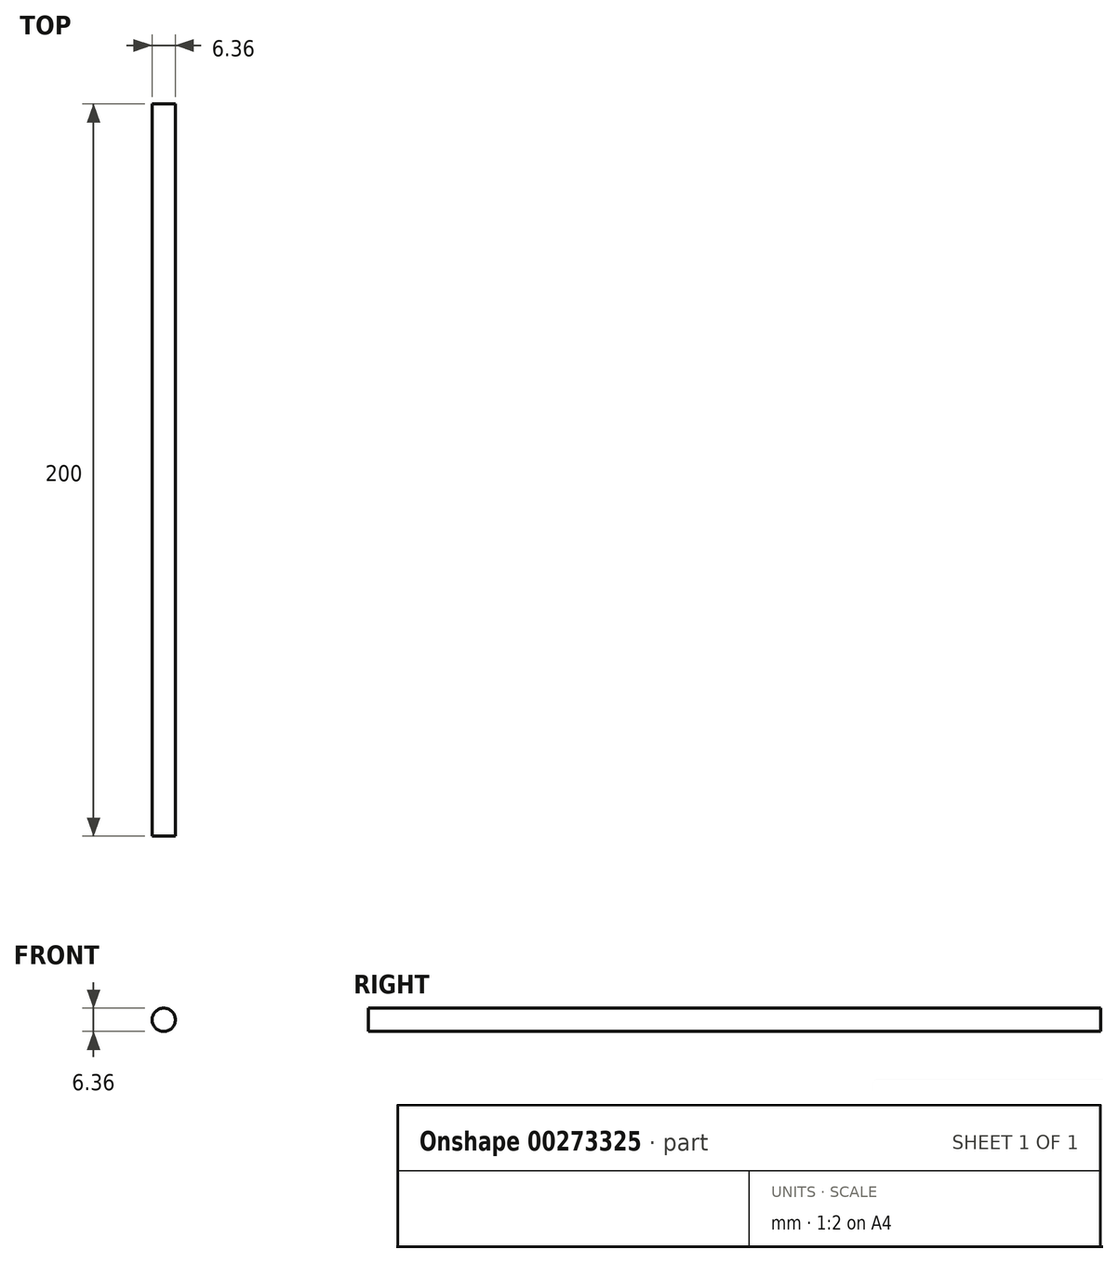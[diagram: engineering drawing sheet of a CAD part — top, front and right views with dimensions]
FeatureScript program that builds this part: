
annotation { "Feature Type Name" : "Feature", "Feature Type Description" : "" }
export const myFeature = defineFeature(function(context is Context, id is Id, definition is map)
    precondition{}
    {
        {
            var Q0;
            Q0=qCreatedBy(makeId("Front.planeOp"),FACE);
            var sketch = newSketch(context, id + "F0", { "sketchPlane" : qUnion([Q0])});
            skCircle(sketch, "E0", {"center": v(0, 0) * mm, "radius": 3.18 * mm});
            skSolve(sketch);
        }
        {
            var Q0;
            Q0=makeQuery(id+"F0.imprint","IMPRINT",FACE,{"disambiguationData":[TD([[makeQuery(id+"F0.imprint","IMPRINT",EDGE,{"derivedFrom":sQuery(id+"F0.wireOp",EDGE,"E0")}),1.0]])]});
            extrude(context, id + "F1", {"entities" : qUnion([Q0]), "depth" : 200 * mm});
        }
    });
